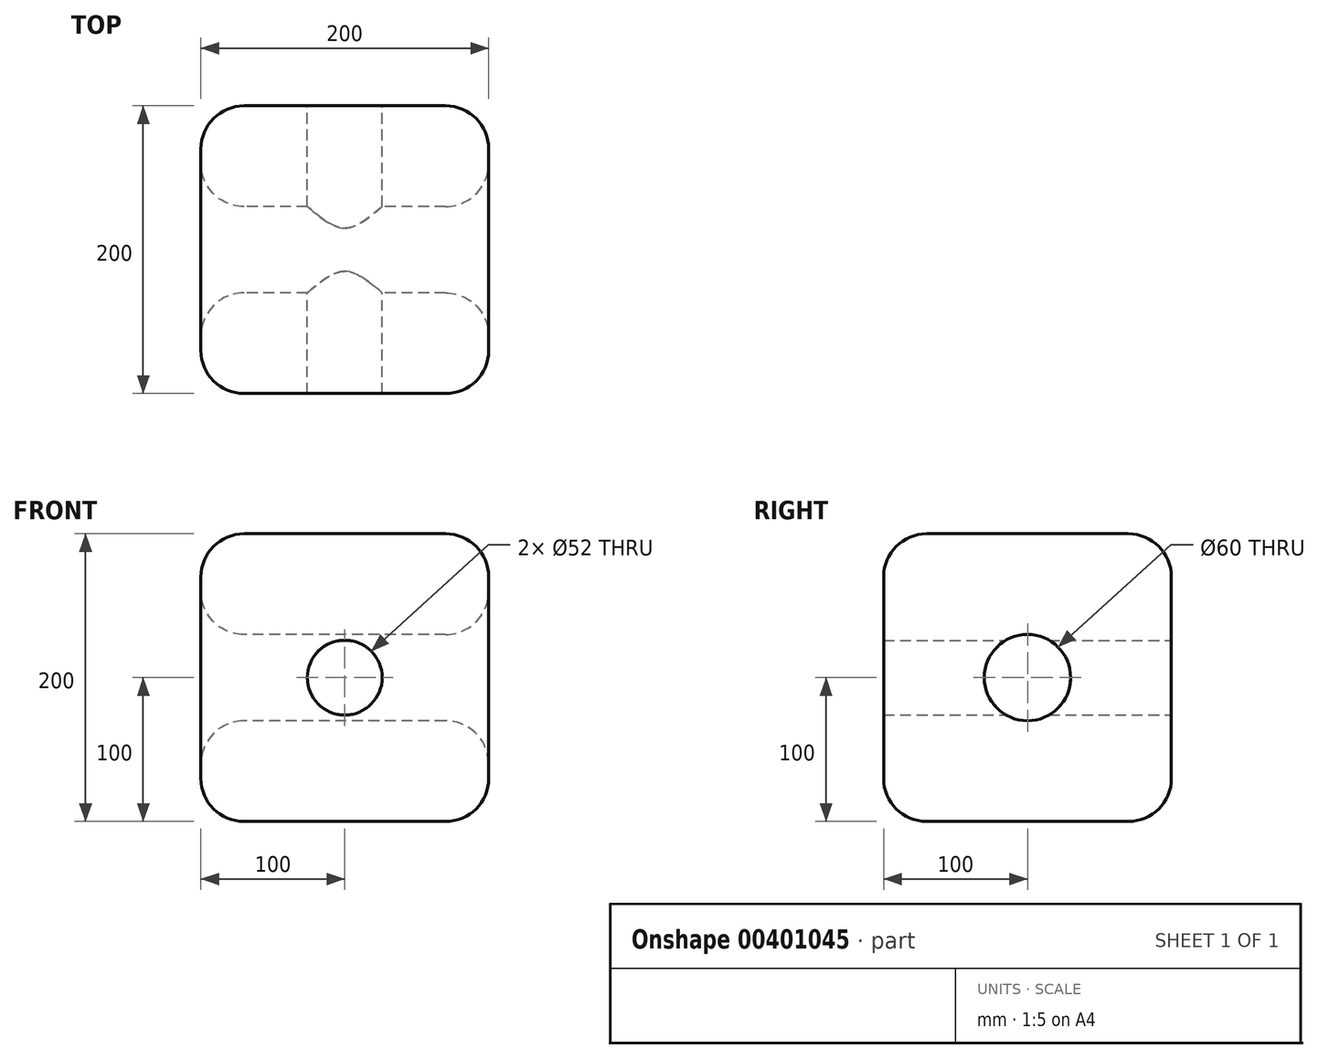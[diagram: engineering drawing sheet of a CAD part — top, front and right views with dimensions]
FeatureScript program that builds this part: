
annotation { "Feature Type Name" : "Feature", "Feature Type Description" : "" }
export const myFeature = defineFeature(function(context is Context, id is Id, definition is map)
    precondition{}
    {
        {
            var Q0;
            Q0=qCreatedBy(makeId("Top.planeOp"),FACE);
            var sketch = newSketch(context, id + "F0", { "sketchPlane" : qUnion([Q0])});
            skLineSegment(sketch, "E0.bottom", {"start": v(-100, 100) * mm, "end": v(100, 100) * mm});
            skLineSegment(sketch, "E0.top", {"start": v(-100, -100) * mm, "end": v(100, -100) * mm});
            skLineSegment(sketch, "E0.left", {"start": v(-100, 100) * mm, "end": v(-100, -100) * mm});
            skLineSegment(sketch, "E0.right", {"start": v(100, 100) * mm, "end": v(100, -100) * mm});
            skSolve(sketch);
        }
        {
            var Q0;
            Q0=makeQuery(id+"F0.imprint","IMPRINT",FACE,{"disambiguationData":[TD([[makeQuery(id+"F0.imprint","IMPRINT",EDGE,{"derivedFrom":sQuery(id+"F0.wireOp",EDGE,"E0.bottom")}),-1.0]])]});
            extrude(context, id + "F1", {"entities" : qUnion([Q0]), "depth" : 200 * mm});
        }
        {
            var Q0;
            Q0=makeQuery(id+"F1.opExtrude","SWEPT_FACE",FACE,{"disambiguationData":[OSD([sQuery(id+"F0.wireOp",EDGE,"E0.left")])]});
            var sketch = newSketch(context, id + "F2", { "sketchPlane" : qUnion([Q0])});
            skCircle(sketch, "E1", {"center": v(0, 100) * mm, "radius": 30 * mm});
            skSolve(sketch);
        }
        {
            var Q0;
            Q0=makeQuery(id+"F2.imprint","IMPRINT",FACE,{"disambiguationData":[TD([[makeQuery(id+"F2.imprint","IMPRINT",EDGE,{"derivedFrom":sQuery(id+"F2.wireOp",EDGE,"E1")}),1.0]])]});
            extrude(context, id + "F3", {"entities" : qUnion([Q0]), "operationType" : NewBodyOperationType.REMOVE, "endBound" : BoundingType.THROUGH_ALL, "oppositeDirection" : true, "depth" : 25 * mm});
        }
        {
            var Q0;
            Q0=makeQuery(id+"F1.opExtrude","SWEPT_FACE",FACE,{"disambiguationData":[OSD([sQuery(id+"F0.wireOp",EDGE,"E0.bottom")])]});
            var Q1;
            Q1=makeQuery(id+"F1.opExtrude","CAP_FACE",FACE,{"disambiguationData":[OSD([sQuery(id+"F0.wireOp",EDGE,"E0.bottom"),sQuery(id+"F0.wireOp",EDGE,"E0.top"),sQuery(id+"F0.wireOp",EDGE,"E0.left"),sQuery(id+"F0.wireOp",EDGE,"E0.right")])],"isStart":false});
            var Q2;
            Q2=makeQuery(id+"F1.opExtrude","SWEPT_FACE",FACE,{"disambiguationData":[OSD([sQuery(id+"F0.wireOp",EDGE,"E0.left")])]});
            var Q3;
            Q3=makeQuery(id+"F1.opExtrude","SWEPT_FACE",FACE,{"disambiguationData":[OSD([sQuery(id+"F0.wireOp",EDGE,"E0.top")])]});
            var Q4;
            Q4=makeQuery(id+"F1.opExtrude","SWEPT_FACE",FACE,{"disambiguationData":[OSD([sQuery(id+"F0.wireOp",EDGE,"E0.right")])]});
            var Q5;
            Q5=makeQuery(id+"F1.opExtrude","CAP_FACE",FACE,{"disambiguationData":[OSD([sQuery(id+"F0.wireOp",EDGE,"E0.bottom"),sQuery(id+"F0.wireOp",EDGE,"E0.top"),sQuery(id+"F0.wireOp",EDGE,"E0.left"),sQuery(id+"F0.wireOp",EDGE,"E0.right")])],"isStart":true});
            fillet(context, id + "F4", {"entities" : qUnion([Q0, Q1, Q2, Q3, Q4, Q5]), "radius" : 30 * mm, "tangentPropagation" : true, "allowEdgeOverflow" : false});
        }
        {
            var Q0;
            Q0=makeQuery(id+"F1.opExtrude","SWEPT_FACE",FACE,{"disambiguationData":[OSD([sQuery(id+"F0.wireOp",EDGE,"E0.bottom")])]});
            var sketch = newSketch(context, id + "F5", { "sketchPlane" : qUnion([Q0])});
            skCircle(sketch, "E2", {"center": v(0, 100) * mm, "radius": 26 * mm});
            skSolve(sketch);
        }
        {
            var Q0;
            Q0=makeQuery(id+"F5.imprint","IMPRINT",FACE,{"disambiguationData":[TD([[makeQuery(id+"F5.imprint","IMPRINT",EDGE,{"derivedFrom":sQuery(id+"F5.wireOp",EDGE,"E2")}),1.0]])]});
            extrude(context, id + "F6", {"entities" : qUnion([Q0]), "operationType" : NewBodyOperationType.REMOVE, "endBound" : BoundingType.THROUGH_ALL, "oppositeDirection" : true, "depth" : 25 * mm});
        }
    });
